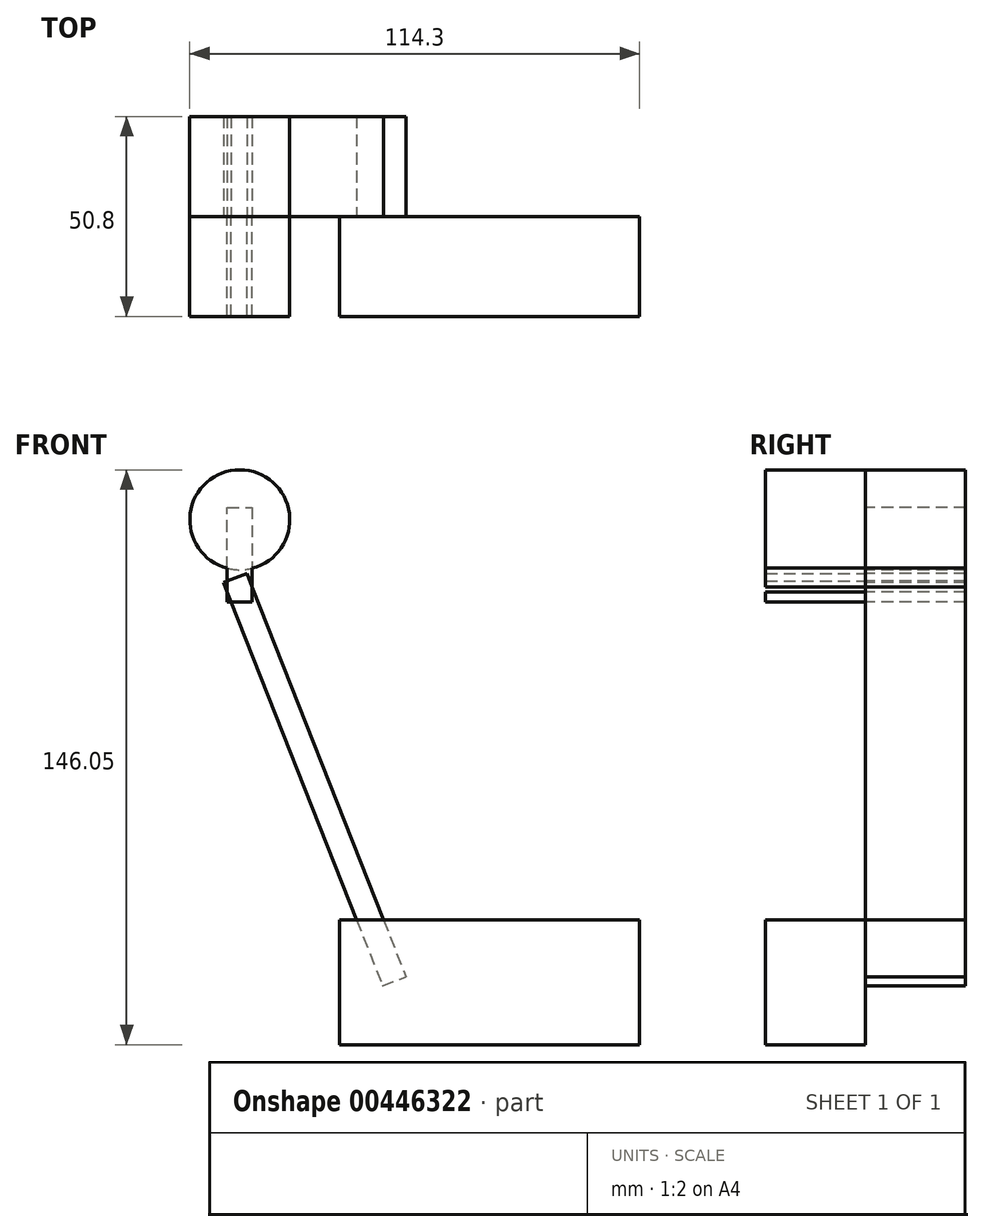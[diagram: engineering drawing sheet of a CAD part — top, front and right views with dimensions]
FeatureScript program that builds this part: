
annotation { "Feature Type Name" : "Feature", "Feature Type Description" : "" }
export const myFeature = defineFeature(function(context is Context, id is Id, definition is map)
    precondition{}
    {
        {
            var Q0;
            Q0=qCreatedBy(makeId("Front.planeOp"),FACE);
            var sketch = newSketch(context, id + "F0", { "sketchPlane" : qUnion([Q0])});
            skCircle(sketch, "E0", {"center": v(0, 0) * mm, "radius": 12.7 * mm});
            skLineSegment(sketch, "E1.bottom", {"start": v(25.4, -127) * mm, "end": v(101.6, -127) * mm});
            skLineSegment(sketch, "E1.top", {"start": v(25.4, -133.35) * mm, "end": v(101.6, -133.35) * mm});
            skLineSegment(sketch, "E1.left", {"start": v(25.4, -127) * mm, "end": v(25.4, -133.35) * mm});
            skLineSegment(sketch, "E1.right", {"start": v(101.6, -127) * mm, "end": v(101.6, -133.35) * mm});
            skPoint(sketch, "E2", {"position": v(101.6, -127) * mm});
            skLineSegment(sketch, "E3", {"start": v(3.18, 3.18) * mm, "end": v(3.18, -20.9) * mm});
            skLineSegment(sketch, "E4", {"start": v(1.79, -13.61) * mm, "end": v(42.22, -116.09) * mm});
            skLineSegment(sketch, "E5", {"start": v(101.6, -127) * mm, "end": v(101.6, -101.6) * mm});
            skLineSegment(sketch, "E6", {"start": v(101.6, -101.6) * mm, "end": v(25.4, -101.6) * mm});
            skPoint(sketch, "E7", {"position": v(88.9, -114.3) * mm});
            skLineSegment(sketch, "E8", {"start": v(1.79, -13.61) * mm, "end": v(-4.12, -15.94) * mm});
            skLineSegment(sketch, "E9", {"start": v(-4.12, -15.94) * mm, "end": v(36.31, -118.42) * mm});
            skLineSegment(sketch, "E10", {"start": v(36.31, -118.42) * mm, "end": v(42.22, -116.09) * mm});
            skLineSegment(sketch, "E11", {"start": v(3.18, -20.9) * mm, "end": v(-3.17, -20.9) * mm});
            skLineSegment(sketch, "E12", {"start": v(-3.17, -20.9) * mm, "end": v(-3.17, 3.18) * mm});
            skLineSegment(sketch, "E13", {"start": v(-3.17, 3.18) * mm, "end": v(3.17, 3.18) * mm});
            skLineSegment(sketch, "E14", {"start": v(-140.42, 38.53) * mm, "end": v(-134.07, 38.53) * mm, "construction": true});
            skLineSegment(sketch, "E15", {"start": v(-3.17, 0) * mm, "end": v(3.17, 0) * mm, "construction": true});
            skLineSegment(sketch, "E16", {"start": v(-3.17, -17.73) * mm, "end": v(3.18, -17.73) * mm, "construction": true});
            skLineSegment(sketch, "E17", {"start": v(2.95, -16.56) * mm, "end": v(-2.95, -18.9) * mm, "construction": true});
            skLineSegment(sketch, "E18", {"start": v(41.05, -113.13) * mm, "end": v(35.15, -115.47) * mm, "construction": true});
            skLineSegment(sketch, "E19", {"start": v(28.58, -127) * mm, "end": v(28.58, -133.35) * mm, "construction": true});
            skLineSegment(sketch, "E20", {"start": v(-138.75, 19.03) * mm, "end": v(-135.58, 19.03) * mm, "construction": true});
            skLineSegment(sketch, "E21", {"start": v(0, 3.18) * mm, "end": v(0, 0) * mm, "construction": true});
            skLineSegment(sketch, "E22", {"start": v(0, -20.9) * mm, "end": v(0, -17.73) * mm, "construction": true});
            skLineSegment(sketch, "E23", {"start": v(-1.17, -14.78) * mm, "end": v(0, -17.73) * mm, "construction": true});
            skLineSegment(sketch, "E24", {"start": v(39.27, -117.25) * mm, "end": v(38.1, -114.3) * mm, "construction": true});
            skLineSegment(sketch, "E25", {"start": v(25.4, -130.17) * mm, "end": v(28.58, -130.17) * mm, "construction": true});
            skLineSegment(sketch, "E26", {"start": v(25.4, -127) * mm, "end": v(25.4, -101.6) * mm});
            skPoint(sketch, "E27", {"position": v(38.1, -114.3) * mm});
            skLineSegment(sketch, "E28", {"start": v(38.1, -114.3) * mm, "end": v(88.9, -114.3) * mm, "construction": true});
            skSolve(sketch);
        }
        {
            var Q0;
            {var subQ0=sQuery(id+"F0.wireOp",EDGE,"E13");Q0=makeQuery(id+"F0.imprint","IMPRINT",FACE,{"disambiguationData":[TD([[makeQuery(id+"F0.imprint","IMPRINT",EDGE,{"derivedFrom":subQ0}),-1.0]])]});}
            var Q1;
            {var subQ0=sQuery(id+"F0.wireOp",EDGE,"E12");var subQ1=sQuery(id+"F0.wireOp",EDGE,"E0");var subQ2=makeQuery(id+"F0.imprint","INTERSECT",VERTEX,{"derivedFrom":[subQ1,subQ0]});Q1=makeQuery(id+"F0.imprint","IMPRINT",FACE,{"disambiguationData":[TD([[makeQuery(id+"F0.imprint","IMPRINT",EDGE,{"disambiguationData":[TD([[subQ2,-1.0]])],"derivedFrom":subQ1}),-1.0]])]});}
            var Q2;
            {var subQ1=sQuery(id+"F0.wireOp",EDGE,"E8");var subQ3=sQuery(id+"F0.wireOp",EDGE,"E0");var subQ4=makeQuery(id+"F0.imprint","INTERSECT",VERTEX,{"derivedFrom":[subQ3,subQ1]});Q2=makeQuery(id+"F0.imprint","IMPRINT",FACE,{"disambiguationData":[TD([[makeQuery(id+"F0.imprint","IMPRINT",EDGE,{"disambiguationData":[TD([[subQ4,-1.0]])],"derivedFrom":subQ3}),-1.0]])]});}
            var Q3;
            {var subQ0=sQuery(id+"F0.wireOp",EDGE,"E3");var subQ1=sQuery(id+"F0.wireOp",EDGE,"E0");var subQ2=makeQuery(id+"F0.imprint","INTERSECT",VERTEX,{"derivedFrom":[subQ1,subQ0]});Q3=makeQuery(id+"F0.imprint","IMPRINT",FACE,{"disambiguationData":[TD([[makeQuery(id+"F0.imprint","IMPRINT",EDGE,{"disambiguationData":[TD([[subQ2,1.0]])],"derivedFrom":subQ1}),-1.0]])]});}
            var Q4;
            {var subQ0=sQuery(id+"F0.wireOp",EDGE,"E8");var subQ1=sQuery(id+"F0.wireOp",EDGE,"E0");var subQ2=makeQuery(id+"F0.imprint","INTERSECT",VERTEX,{"derivedFrom":[subQ1,subQ0]});Q4=makeQuery(id+"F0.imprint","IMPRINT",FACE,{"disambiguationData":[TD([[makeQuery(id+"F0.imprint","IMPRINT",EDGE,{"disambiguationData":[TD([[subQ2,-1.0]])],"derivedFrom":subQ1}),1.0]])]});}
            var Q5;
            {var subQ0=sQuery(id+"F0.wireOp",EDGE,"E12");var subQ1=sQuery(id+"F0.wireOp",EDGE,"E9");var subQ2=makeQuery(id+"F0.imprint","INTERSECT",VERTEX,{"derivedFrom":[subQ1,subQ0]});Q5=makeQuery(id+"F0.imprint","IMPRINT",FACE,{"disambiguationData":[TD([[makeQuery(id+"F0.imprint","IMPRINT",EDGE,{"disambiguationData":[TD([[subQ2,-1.0]])],"derivedFrom":subQ1}),-1.0]])]});}
            extrude(context, id + "F1", {"entities" : qUnion([Q0, Q1, Q2, Q3, Q4, Q5]), "depth" : 25.4 * mm, "offsetDistance" : 25.4 * mm});
        }
        {
            var Q0;
            {var subQ3=sQuery(id+"F0.wireOp",EDGE,"E11");var subQ6=sQuery(id+"F0.wireOp",EDGE,"E3");var subQ9=makeQuery(id+"F0.imprint","INTERSECT",VERTEX,{"derivedFrom":[subQ6,subQ3]});Q0=makeQuery(id+"F0.imprint","IMPRINT",FACE,{"disambiguationData":[TD([[makeQuery(id+"F0.imprint","IMPRINT",EDGE,{"disambiguationData":[TD([[subQ9,1.0]])],"derivedFrom":subQ6}),1.0]])]});}
            var Q1;
            {var subQ3=sQuery(id+"F0.wireOp",EDGE,"E0");var subQ5=sQuery(id+"F0.wireOp",EDGE,"E8");var subQ6=makeQuery(id+"F0.imprint","INTERSECT",VERTEX,{"derivedFrom":[subQ3,subQ5]});Q1=makeQuery(id+"F0.imprint","IMPRINT",FACE,{"disambiguationData":[TD([[makeQuery(id+"F0.imprint","IMPRINT",EDGE,{"disambiguationData":[TD([[subQ6,-1.0]])],"derivedFrom":subQ3}),-1.0]])]});}
            var Q2;
            {var subQ0=sQuery(id+"F0.wireOp",EDGE,"E9");var subQ1=sQuery(id+"F0.wireOp",EDGE,"E8");var subQ2=makeQuery(id+"F0.imprint","INTERSECT",VERTEX,{"derivedFrom":[subQ1,subQ0]});Q2=makeQuery(id+"F0.imprint","IMPRINT",FACE,{"disambiguationData":[TD([[makeQuery(id+"F0.imprint","IMPRINT",EDGE,{"disambiguationData":[TD([[subQ2,1.0]])],"derivedFrom":subQ1}),1.0]])]});}
            var Q3;
            {var subQ0=sQuery(id+"F0.wireOp",EDGE,"E8");var subQ1=sQuery(id+"F0.wireOp",EDGE,"E0");var subQ2=makeQuery(id+"F0.imprint","INTERSECT",VERTEX,{"derivedFrom":[subQ1,subQ0]});Q3=makeQuery(id+"F0.imprint","IMPRINT",FACE,{"disambiguationData":[TD([[makeQuery(id+"F0.imprint","IMPRINT",EDGE,{"disambiguationData":[TD([[subQ2,-1.0]])],"derivedFrom":subQ1}),1.0]])]});}
            var Q4;
            {var subQ0=sQuery(id+"F0.wireOp",EDGE,"E10");Q4=makeQuery(id+"F0.imprint","IMPRINT",FACE,{"disambiguationData":[TD([[makeQuery(id+"F0.imprint","IMPRINT",EDGE,{"derivedFrom":subQ0}),1.0]])]});}
            extrude(context, id + "F2", {"entities" : qUnion([Q0, Q1, Q2, Q3, Q4]), "oppositeDirection" : true, "depth" : 25.4 * mm, "offsetDistance" : 25.4 * mm});
        }
        {
            var Q0;
            Q0=makeQuery(id+"F0.imprint","IMPRINT",FACE,{"disambiguationData":[TD([[makeQuery(id+"F0.imprint","IMPRINT",EDGE,{"derivedFrom":sQuery(id+"F0.wireOp",EDGE,"E1.bottom")}),1.0]])]});
            var Q1;
            {var subQ0=sQuery(id+"F0.wireOp",EDGE,"E10");Q1=makeQuery(id+"F0.imprint","IMPRINT",FACE,{"disambiguationData":[TD([[makeQuery(id+"F0.imprint","IMPRINT",EDGE,{"derivedFrom":subQ0}),1.0]])]});}
            var Q2;
            Q2=makeQuery(id+"F0.imprint","IMPRINT",FACE,{"disambiguationData":[TD([[makeQuery(id+"F0.imprint","IMPRINT",EDGE,{"derivedFrom":sQuery(id+"F0.wireOp",EDGE,"E1.bottom")}),-1.0]])]});
            extrude(context, id + "F3", {"entities" : qUnion([Q0, Q1, Q2]), "depth" : 25.4 * mm, "offsetDistance" : 25.4 * mm});
        }
    });
